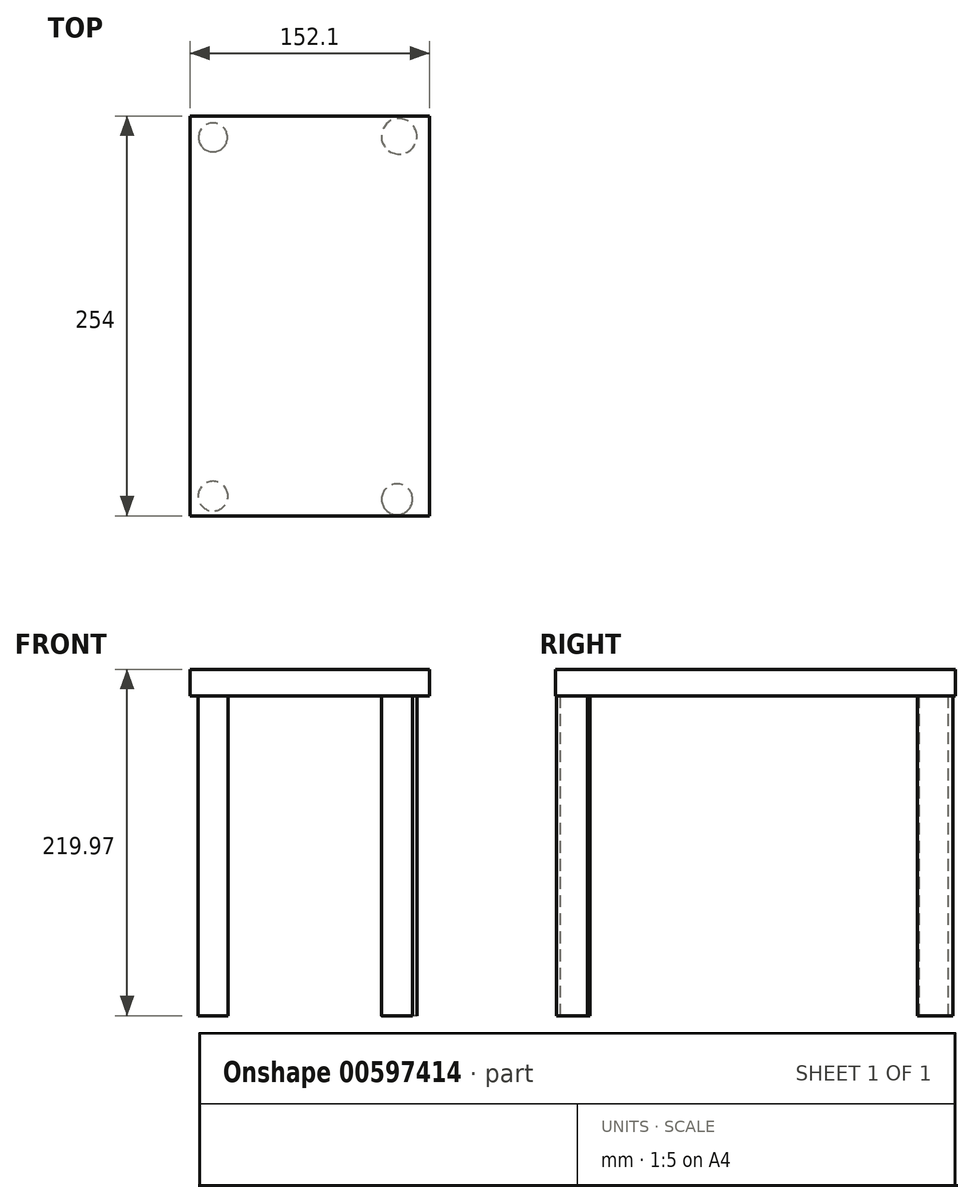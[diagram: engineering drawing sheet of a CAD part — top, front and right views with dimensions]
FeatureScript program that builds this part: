
annotation { "Feature Type Name" : "Feature", "Feature Type Description" : "" }
export const myFeature = defineFeature(function(context is Context, id is Id, definition is map)
    precondition{}
    {
        {
            var Q0;
            Q0=qCreatedBy(makeId("Front.planeOp"),FACE);
            var sketch = newSketch(context, id + "F0", { "sketchPlane" : qUnion([Q0])});
            skLineSegment(sketch, "E0.bottom", {"start": v(-75.44, 6.7) * mm, "end": v(76.66, 6.7) * mm});
            skLineSegment(sketch, "E0.top", {"start": v(-75.44, -10.06) * mm, "end": v(76.66, -10.06) * mm});
            skLineSegment(sketch, "E0.left", {"start": v(-75.44, 6.7) * mm, "end": v(-75.44, -10.06) * mm});
            skLineSegment(sketch, "E0.right", {"start": v(76.66, 6.7) * mm, "end": v(76.66, -10.06) * mm});
            skSolve(sketch);
        }
        {
            var Q0;
            Q0=makeQuery(id+"F0.imprint","IMPRINT",FACE,{"disambiguationData":[TD([[makeQuery(id+"F0.imprint","IMPRINT",EDGE,{"derivedFrom":sQuery(id+"F0.wireOp",EDGE,"E0.bottom")}),-1.0]])]});
            extrude(context, id + "F1", {"entities" : qUnion([Q0]), "depth" : 254 * mm, "offsetDistance" : 25.4 * mm});
        }
        {
            var Q0;
            Q0=makeQuery(id+"F1.opExtrude","SWEPT_FACE",FACE,{"disambiguationData":[OSD([sQuery(id+"F0.wireOp",EDGE,"E0.top")])]});
            var sketch = newSketch(context, id + "F2", { "sketchPlane" : qUnion([Q0])});
            skCircle(sketch, "E1", {"center": v(-60.86, 241.45) * mm, "radius": 9.46 * mm});
            skCircle(sketch, "E2", {"center": v(-60.86, 13.61) * mm, "radius": 9.17 * mm});
            skCircle(sketch, "E3", {"center": v(57.35, 12.95) * mm, "radius": 11.28 * mm});
            skCircle(sketch, "E4", {"center": v(56.03, 243.43) * mm, "radius": 9.82 * mm});
            skSolve(sketch);
        }
        {
            var Q0;
            Q0 = qSketchRegion(id + "F2", true);
            extrude(context, id + "F3", {"entities" : qUnion([Q0]), "operationType" : NewBodyOperationType.ADD, "depth" : 203.2 * mm, "offsetDistance" : 25.4 * mm});
        }
    });
